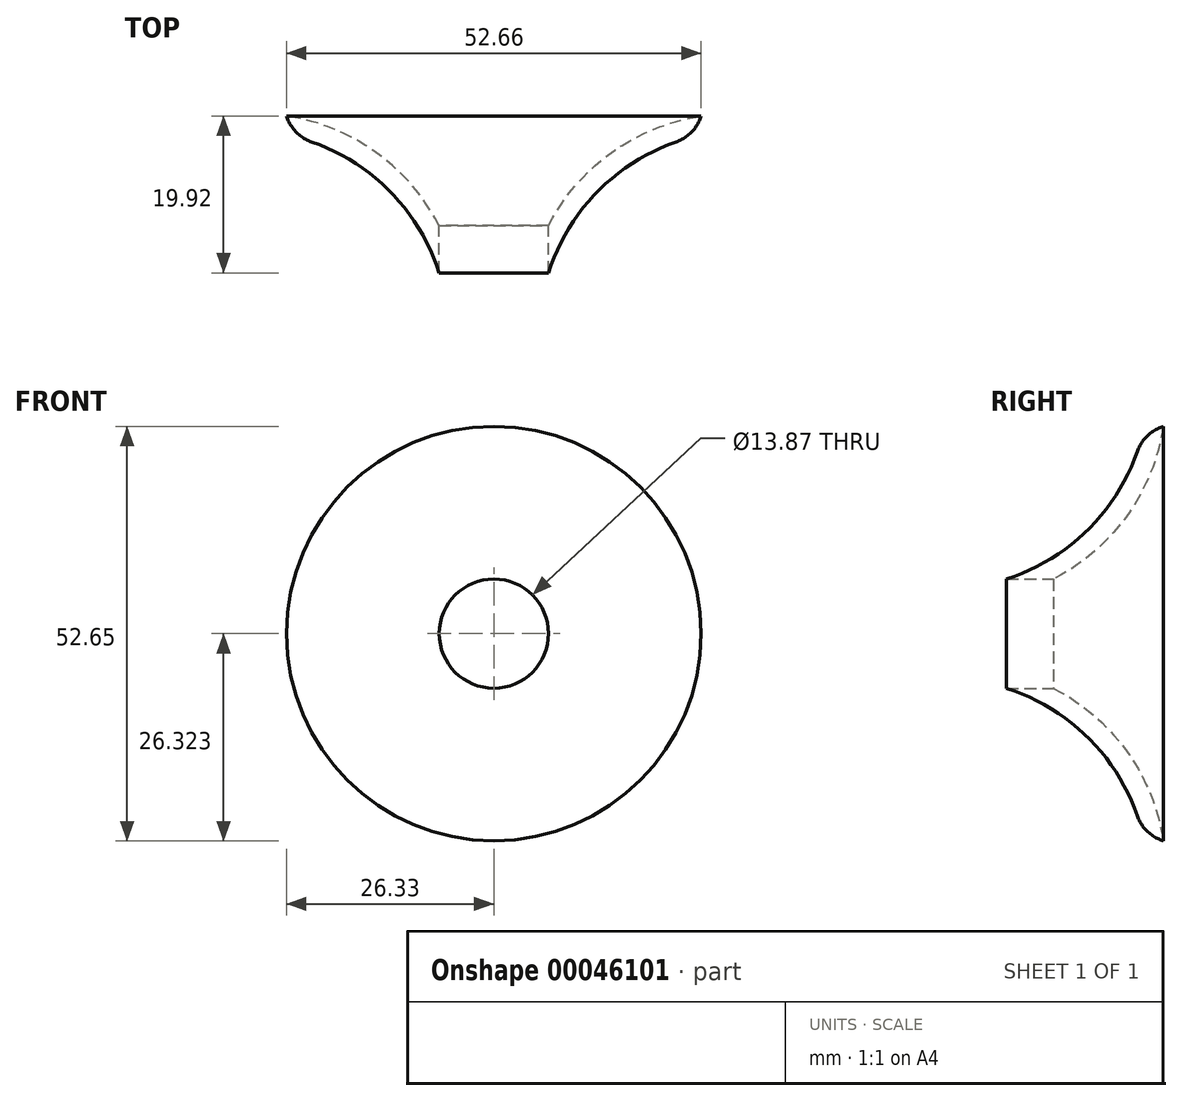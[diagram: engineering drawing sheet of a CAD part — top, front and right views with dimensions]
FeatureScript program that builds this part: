
annotation { "Feature Type Name" : "Feature", "Feature Type Description" : "" }
export const myFeature = defineFeature(function(context is Context, id is Id, definition is map)
    precondition{}
    {
        {
            var Q0;
            Q0=qCreatedBy(makeId("Right.planeOp"),FACE);
            var sketch = newSketch(context, id + "F0", { "sketchPlane" : qUnion([Q0])});
            skLineSegment(sketch, "E0", {"start": v(0.11, -0.06) * mm, "end": v(-19.81, -0.06) * mm});
            skLineSegment(sketch, "E1", {"start": v(0.11, -26.38) * mm, "end": v(-2.29, -26.38) * mm});
            skArc(sketch, "E2", {"start": v(-2.29, -26.38) * mm, "mid": v(-8.43, -14.32) * mm, "end": v(-19.81, -7) * mm});
            skLineSegment(sketch, "E3", {"start": v(-27.7, -31.73) * mm, "end": v(-25.79, -30.29) * mm});
            skArc(sketch, "E4", {"start": v(0.11, -26.38) * mm, "mid": v(-4.52, -15) * mm, "end": v(-13.82, -7) * mm});
            skLineSegment(sketch, "E5", {"start": v(-19.81, -7) * mm, "end": v(-13.82, -7) * mm});
            skSolve(sketch);
        }
        {
            var Q0;
            Q0=makeQuery(id+"F0.imprint","IMPRINT",FACE,{"disambiguationData":[TD([[makeQuery(id+"F0.imprint","IMPRINT",EDGE,{"derivedFrom":sQuery(id+"F0.wireOp",EDGE,"E1")}),-1.0]])]});
            var Q1;
            Q1=sQuery(id+"F0.wireOp",EDGE,"E0");
            revolve(context, id + "F1", {"entities" : qUnion([Q0]), "axis" : qUnion([Q1]), "revolveType" : RevolveType.FULL});
        }
        {
            var Q0;
            Q0=makeQuery(id+"F1.opRevolve","SWEPT_EDGE",EDGE,{"disambiguationData":[OSD([sQuery(id+"F0.wireOp",EDGE,"E1"),sQuery(id+"F0.wireOp",EDGE,"E2")])]});
            fillet(context, id + "F2", {"entities" : qUnion([Q0]), "radius" : 5.08 * mm, "tangentPropagation" : true, "defaultsChanged" : false, "vertexSettings" : [], "allowEdgeOverflow" : false});
        }
    });
